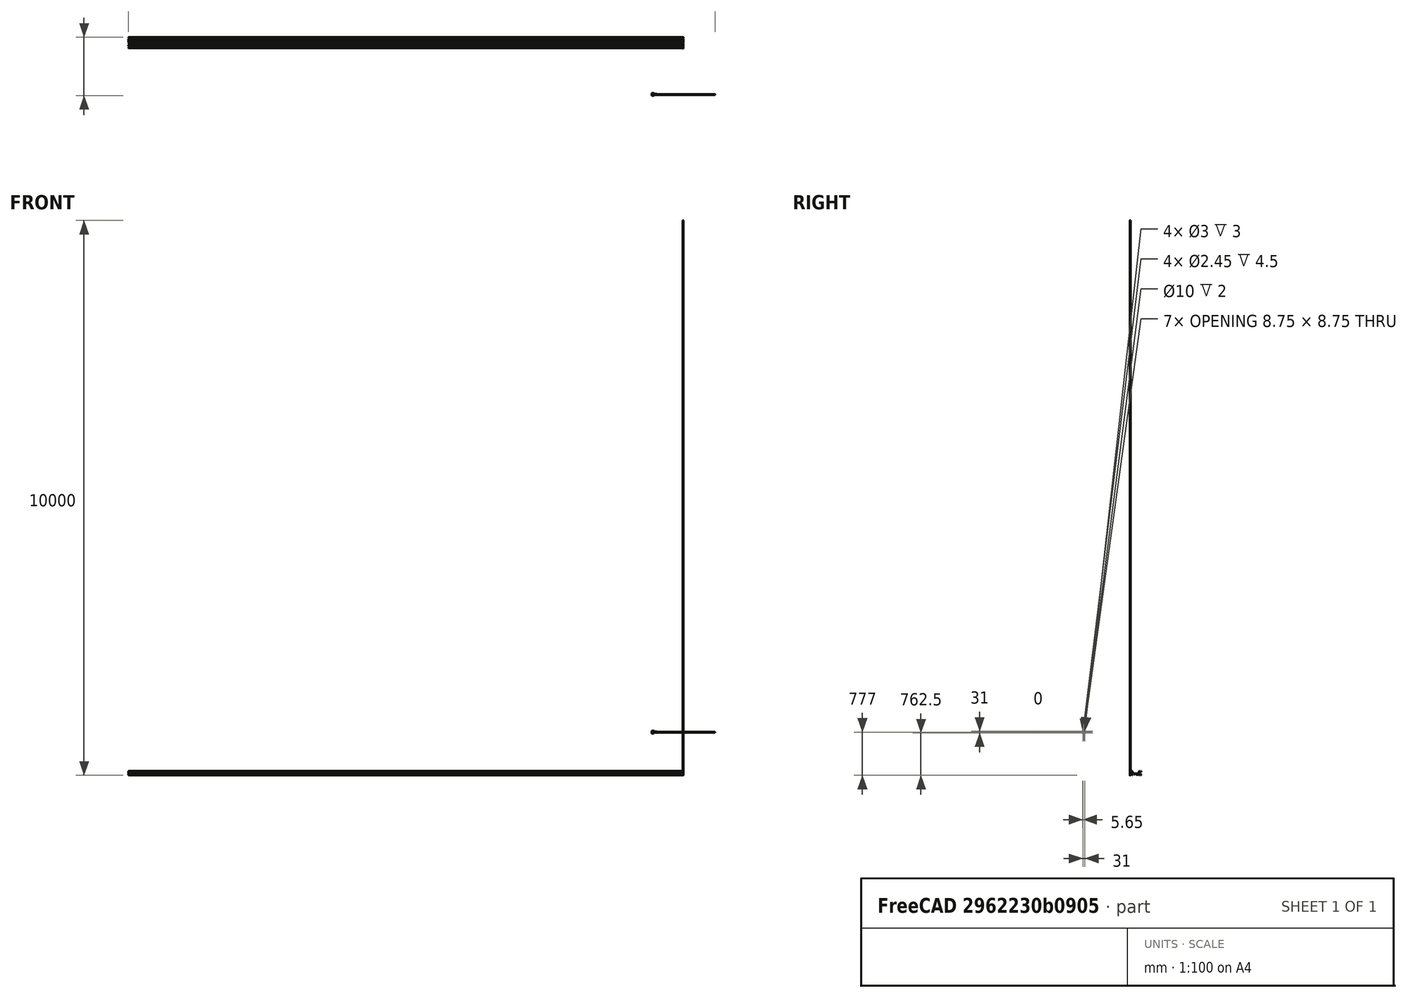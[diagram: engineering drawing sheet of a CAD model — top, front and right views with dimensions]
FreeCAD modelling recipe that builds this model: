
FCSTD DOCUMENT  (FreeCAD 0.14R3702 (Git))
Label: left_slide_rail_flange_mount_subassembly
License: CC-BY 3.0
LicenseURL: http://creativecommons.org/licenses/by/3.0/
objects: Mesh::Feature×3, Sketcher::SketchObject×2, PartDesign::Pocket×2, Part::Feature×2, Part::Cylinder×1
note: 9 computed .brp shape members not serialized (recipe doc carries the construction recipe); baked Part::Feature solids carry a one-line shape summary decoded from their .brp

FEATURE [Sketcher::SketchObject] Sketch
  Placement = pos=(-475,-836,778) rot=(0.707107,0,-0.707107;3.14159rad)
  sketch-geometry (1):
    g0: Circle CenterX=0 CenterY=0 CenterZ=0 NormalX=0 NormalY=0 NormalZ=1 Radius=5
  constraints (2):
    c: Coincident(g0,g-1)
    c: Radius(g0) = 5
FEATURE [PartDesign::Pocket] Pocket
  Length = 5
  Placement = pos=(-475,-836,778) rot=(0,1,0;1.5708rad)
  Sketch = -> Sketch
  Type = 1
FEATURE [Part::Feature] Part__Feature  label="x-axis-helical-coupler"
  Placement = pos=(-494,-835,777) rot=(0,0,1;0rad)
  shape: bbox 28 x 20 x 20 mm, 505 faces (baked)
FEATURE [Part::Feature] Part__Feature001  label="x_axis_stepper_motor"
  Placement = pos=(-564,-835,778) rot=(0,1,0;1.5708rad)
  shape: bbox 60.1 x 42.3 x 48 mm, 110 faces (baked)
FEATURE [Sketcher::SketchObject] Sketch001
  Placement = pos=(-460,-958,759) rot=(0.57735,0.57735,0.57735;2.0944rad)
  sketch-geometry (24):
    g0: Circle CenterX=45 CenterY=41 CenterZ=0 NormalX=0 NormalY=0 NormalZ=1 Radius=10
    g1: Circle CenterX=153 CenterY=41 CenterZ=0 NormalX=0 NormalY=0 NormalZ=1 Radius=10
    g2: Circle CenterX=122 CenterY=19 CenterZ=0 NormalX=0 NormalY=0 NormalZ=1 Radius=10
    g3: Circle CenterX=36.5 CenterY=74 CenterZ=0 NormalX=0 NormalY=0 NormalZ=1 Radius=2.5
    g4: Circle CenterX=36.5 CenterY=60 CenterZ=0 NormalX=0 NormalY=0 NormalZ=1 Radius=2.5
    g5: Circle CenterX=5.5 CenterY=74 CenterZ=0 NormalX=0 NormalY=0 NormalZ=1 Radius=2.5
    g6: Circle CenterX=5.5 CenterY=60 CenterZ=0 NormalX=0 NormalY=0 NormalZ=1 Radius=2.5
    g7: Circle CenterX=37 CenterY=19.5 CenterZ=0 NormalX=0 NormalY=0 NormalZ=1 Radius=2.5
    g8: Circle CenterX=37 CenterY=5.5 CenterZ=0 NormalX=0 NormalY=0 NormalZ=1 Radius=2.5
    g9: Circle CenterX=5.5 CenterY=19.5 CenterZ=0 NormalX=0 NormalY=0 NormalZ=1 Radius=2.5
    g10: Circle CenterX=5.5 CenterY=5.5 CenterZ=0 NormalX=0 NormalY=0 NormalZ=1 Radius=2.5
    g11: Circle CenterX=162.5 CenterY=19.5 CenterZ=0 NormalX=0 NormalY=0 NormalZ=1 Radius=2.5
    g12: Circle CenterX=162.5 CenterY=5.5 CenterZ=0 NormalX=0 NormalY=0 NormalZ=1 Radius=2.5
    g13: Circle CenterX=194 CenterY=19.5 CenterZ=0 NormalX=0 NormalY=0 NormalZ=1 Radius=2.5
    g14: Circle CenterX=194 CenterY=5.5 CenterZ=0 NormalX=0 NormalY=0 NormalZ=1 Radius=2.5
    g15: Circle CenterX=162.5 CenterY=74 CenterZ=0 NormalX=0 NormalY=0 NormalZ=1 Radius=2.5
    g16: Circle CenterX=162.5 CenterY=60 CenterZ=0 NormalX=0 NormalY=0 NormalZ=1 Radius=2.5
    g17: Circle CenterX=194 CenterY=74 CenterZ=0 NormalX=0 NormalY=0 NormalZ=1 Radius=2.5
    g18: Circle CenterX=194 CenterY=60 CenterZ=0 NormalX=0 NormalY=0 NormalZ=1 Radius=2.5
    g19: Circle CenterX=107 CenterY=34 CenterZ=0 NormalX=0 NormalY=0 NormalZ=1 Radius=2.5
    g20: Circle CenterX=135 CenterY=36 CenterZ=0 NormalX=0 NormalY=0 NormalZ=1 Radius=2.5
    g21: Circle CenterX=142 CenterY=10 CenterZ=0 NormalX=0 NormalY=0 NormalZ=1 Radius=2.5
    g22: Circle CenterX=77 CenterY=34 CenterZ=0 NormalX=0 NormalY=0 NormalZ=1 Radius=2.5
    g23: Circle CenterX=77 CenterY=14 CenterZ=0 NormalX=0 NormalY=0 NormalZ=1 Radius=2.5
  constraints (68):
    c: Radius(g0) = 10
    c: DistanceX(g-1,g0) = 45
    c: DistanceY(g-1,g0) = 41
    c: Radius(g1) = 10
    c: DistanceX(g-1,g1) = 153
    c: DistanceY(g-1,g1) = 41
    c: Radius(g2) = 10
    c: DistanceX(g-1,g2) = 122
    c: DistanceY(g-1,g2) = 19
    c: Radius(g3) = 2.5
    c: DistanceX(g-1,g3) = 36.5
    c: Equal(g4,g3)
    c: DistanceX(g-1,g4) = 36.5
    c: DistanceY(g-1,g4) = 60
    c: Equal(g4,g5)
    c: DistanceX(g5) = 5.5
    c: DistanceX(g6) = 5.5
    c: DistanceY(g-1,g6) = 60
    c: Equal(g5,g6)
    c: Equal(g6,g9)
    c: Equal(g9,g10)
    c: Equal(g10,g7)
    c: Equal(g7,g8)
    c: Equal(g8,g22)
    c: Equal(g22,g23)
    c: Equal(g23,g19)
    c: Equal(g20,g21)
    c: Equal(g21,g11)
    c: Equal(g11,g12)
    c: Equal(g12,g15)
    c: Equal(g15,g16)
    c: Equal(g16,g17)
    c: Equal(g17,g18)
    c: Equal(g18,g13)
    c: Equal(g13,g14)
    c: DistanceX(g-1,g9) = 5.5
    c: DistanceX(g-1,g10) = 5.5
    c: DistanceX(g7,g9) = -31.5
    c: DistanceX(g8,g10) = -31.5
    c: DistanceY(g9,g10) = -14
    c: DistanceY(g7,g8) = -14
    c: DistanceY(g-1,g8) = 5.5
    c: DistanceY(g-1,g10) = 5.5
    c: DistanceY(g12,g11) = 14
    c: DistanceY(g13,g14) = -14
    c: DistanceY(g-1,g12) = 5.5
    c: DistanceY(g-1,g14) = 5.5
    c: DistanceX(g-1,g11) = 162.5
    c: DistanceX(g-1,g12) = 162.5
    c: DistanceX(g12,g14) = 31.5
    c: DistanceX(g11,g13) = 31.5
    c: DistanceY(g16,g15) = 14
    c: DistanceY(g17,g18) = -14
    c: DistanceX(g16,g18) = 31.5
    c: DistanceX(g15,g17) = 31.5
    c: DistanceX(g-1,g16) = 162.5
    c: DistanceX(g-1,g15) = 162.5
    c: DistanceY(g-1,g16) = 60
    c: DistanceY(g-1,g18) = 60
    c: DistanceY(g-1,g21) = 10
    c: DistanceX(g-1,g21) = 142
    c: DistanceX(g-1,g20) = 135
    c: DistanceY(g21,g20) = 26
    c: DistanceX(g-1,g19) = 107
    c: DistanceY(g-1,g23) = 14
    c: DistanceY(g23,g22) = 20
    c: DistanceX(g19,g22) = -30
    c: DistanceY(g-1,g19) = 34
FEATURE [PartDesign::Pocket] Pocket001
  Length = 5
  Placement = pos=(-466,-958,759) rot=(0,0,1;0rad)
  Sketch = -> Sketch001
  Type = 1
FEATURE [Mesh::Feature] vertical_lead_screw  label="vertical_lead_screw_left"
  Placement = pos=(-472,-866,54) rot=(0,0,1;0rad)
FEATURE [Part::Cylinder] Cylinder  label="left_lead_screw"
  Angle = 360
  Height = 1066.8
  Placement = pos=(-491,-836,778) rot=(0,1,0;1.5708rad)
  Radius = 5.556
FEATURE [Mesh::Feature] lead_screw_flange  label="z-axis-lead-screw-flange-left"
  Placement = pos=(-472,-866,721) rot=(0,0,-1;0.523599rad)
FEATURE [Mesh::Feature] left_slide_rail_flange_mount
  Placement = pos=(-466,-807,759) rot=(0.57735,-0.57735,-0.57735;2.0944rad)
